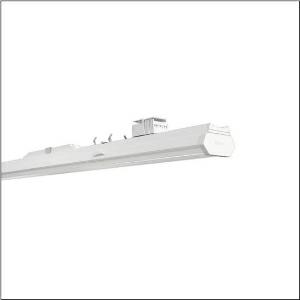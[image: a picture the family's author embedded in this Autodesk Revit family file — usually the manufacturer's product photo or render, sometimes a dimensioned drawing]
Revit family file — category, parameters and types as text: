
# Revit family: licross_r__11_protected_mo_51tp12cn48xf_c165
name_source: partatom
category: Lighting Fixtures
units: mm (PartAtom-declared; Revit-internal decimal feet)

## family parameters
Cut with Voids When Loaded = No
Host = Face
Light Source = No
Part Type = Normal
Room Calculation Point = No
Round Connector Dimension = Use Diameter
Shared = No

## types (1)
- --- (1 x LED, 8180 lm, 49 W, 4000K)
    Apparent Load = 49 VA
    CIE Flux Codes = 73 92 98 99 100
    Color Rendering = 80
    Color Temperature = 4000K
    Default Elevation = 1800 mm
    Description = Licross® 11 Protected MOluminaire insert, length: 1.500mm, width: 90mm, height: 101mm, LED rated luminous flux: 8.180lm, light colour: 840, control gear: ON/OFF Multilumen, CLOi, control gear: ECG Multilumen, with plug, 3-pole, with phase selection, mains connection: 220..240V, AC, 50/60Hz, halogen-free wiring, primary optical cover: cover, of PMMA, light emission: direct with ceiling illumination distribution, protection rating (complete): IP64, insulation class (complete): insulation class I (protective earthing), certification: CE, ENEC, VDE, protection symbol: D if used in an environment with conductive dust loads with corresponding accessories, permissible ambient temperature for indoor applications: -35..+40°C, reducing of maximum allowable ambient temperature of 5°C with ceiling mounting, corresponds to IFS (International Featured Standards) requirements for safety and quality in the food industry, packaging unit: 1 piece
    Height = 92 mm
    Lamp = 1 x LED
    Lamp Light Flux = 8180 lm
    Lamp Power = 49 W
    Lamp count = 1
    Length = 1500 mm
    Luminous efficacy = 167 lm/W
    Manufacturer = Siteco
    ModVariant = No
    Model = 51TP12CN48XF
    Mounting Place = Ceiling
    Mounting Type = Pendant
    Number of Poles = 1
    OnlyDefault = Yes
    Power Factor = 1
    Product Name = Licross® 11 Protected MO
    Product group = luminaire insert
    ProductGroupID = 902
    Protection Class = Protection class I
    Protection Degree = IP 64
    RLX_Detail_Level = 1
    RlxData = <blob elided: 21841 chars, md5=ea1ff248>
    Socket = socket
    Standby Power = 0 W
    System Light Flux = 8180 lm
    System Power = 49 W
    Type Comments = factory setting: luminous flux: 100 % | (A | C | E) | 111 mA
    Type Image = l_1256148.jpg
    URL = http://relux.com
    VarID = @adj_137909
    Voltage = 0 V
    Weight = 0.00 kg
    Width = 88 mm

## geometry (parser evidence)
native form markers: Blend x4, Sweep x11
no freeform markers — native parametric forms only
